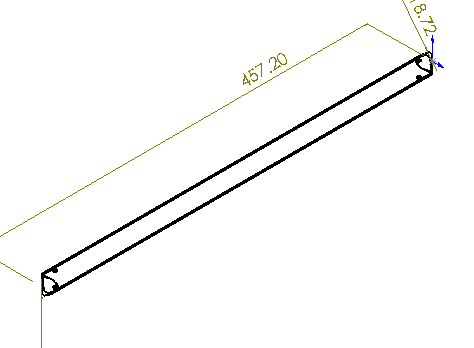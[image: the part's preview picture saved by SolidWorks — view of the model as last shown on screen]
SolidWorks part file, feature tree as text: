
SOLIDWORKS PART (.sldprt)
format: sldprt  version: not decoded by parser v0  size: 197,120 bytes
history: native  units: mm
features: sketch x4, cut_extrude x3, material x1, extrude x1 + 1 further entry (+14 scaffold rows collapsed)
feature tree (24):
  scaffold x14  (default folders/planes/origin — collapsed)
  material  "Material <not specified>"
  "Annotations"  RD3=15.98mm RD2=457.2mm RD1=18.72mm
  sketch  "Sketch1"  dims[D1=7.875mm]
  extrude  "Extrude1"  Depth=457.2mm
  sketch  "Sketch2"  dims[D1=19.05mm]
  cut_extrude  "Cut-Extrude1"  [1 undecoded]
  sketch  "Sketch3"  dims[D1=~8.980256mm]
  cut_extrude  "Cut-Extrude2"  [1 undecoded]
  sketch  "Sketch5"  dims[D1=3.175mm]
  cut_extrude  "Cut-Extrude3"  [1 undecoded]
decode coverage: 5 of 8 modeling features carry decoded parameters; 1 rows unclassified (native names shown)
note: ~ marks probable driven/reference dimensions
note: 3 parameter values undecoded
summary: no parameter record found for 3 features
note: suppression state not decoded; provenance and decode notes live in map.json
